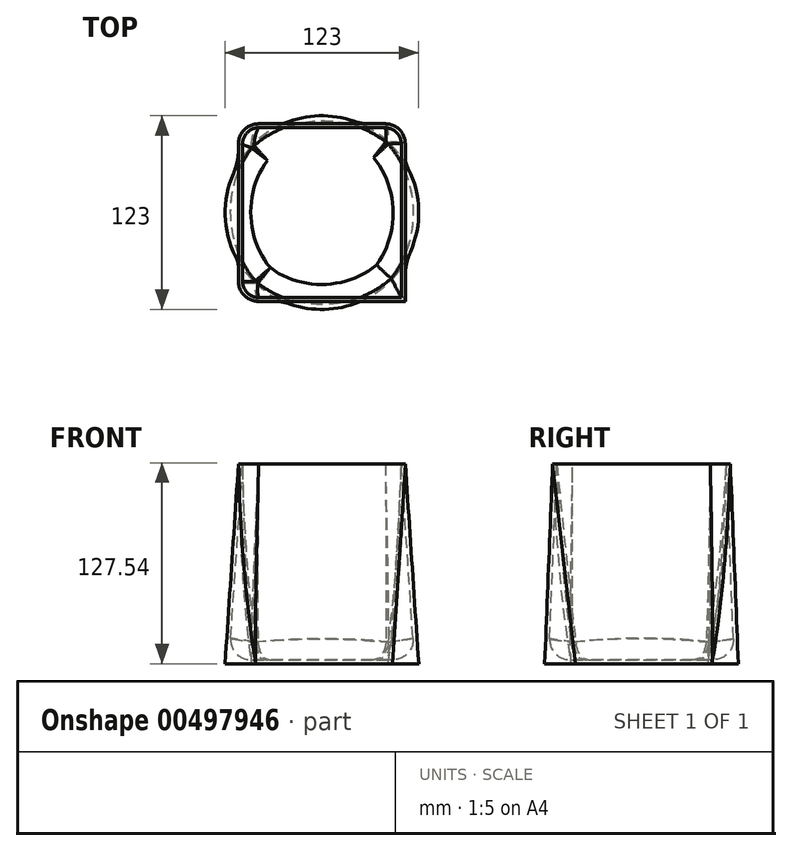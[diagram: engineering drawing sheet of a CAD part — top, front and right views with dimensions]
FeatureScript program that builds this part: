
annotation { "Feature Type Name" : "Feature", "Feature Type Description" : "" }
export const myFeature = defineFeature(function(context is Context, id is Id, definition is map)
    precondition{}
    {
        {
            var Q0;
            Q0=qCreatedBy(makeId("Top.planeOp"),FACE);
            var sketch = newSketch(context, id + "F0", { "sketchPlane" : qUnion([Q0])});
            skCircle(sketch, "E0", {"center": v(0, 0) * mm, "radius": 61.5 * mm});
            skSolve(sketch);
        }
        {
            var Q0;
            Q0=qCreatedBy(makeId("Top.planeOp"),FACE);
            cPlane(context, id + "F1", {"entities" : qUnion([Q0]), "cplaneType" : CPlaneType.OFFSET, "offset" : 127 * mm, "width" : 152.4 * mm, "height" : 152.4 * mm});
        }
        {
            var Q0;
            Q0=qCreatedBy(id+"F1.planeOp",FACE);
            var sketch = newSketch(context, id + "F2", { "sketchPlane" : qUnion([Q0])});
            skLineSegment(sketch, "E1.bottom", {"start": v(52.96, 56.4) * mm, "end": v(-52.96, 56.4) * mm});
            skLineSegment(sketch, "E1.top", {"start": v(52.96, -56.4) * mm, "end": v(-52.96, -56.4) * mm});
            skLineSegment(sketch, "E1.left", {"start": v(52.96, 56.4) * mm, "end": v(52.96, -56.4) * mm});
            skLineSegment(sketch, "E1.right", {"start": v(-52.96, 56.4) * mm, "end": v(-52.96, -56.4) * mm});
            skPoint(sketch, "E1.middle", {"position": v(0, 0) * mm});
            skSolve(sketch);
        }
        {
            var Q0;
            Q0=makeQuery(id+"F2.imprint","IMPRINT",FACE,{"disambiguationData":[TD([[makeQuery(id+"F2.imprint","IMPRINT",EDGE,{"derivedFrom":sQuery(id+"F2.wireOp",EDGE,"E1.bottom")}),1.0]])]});
            var Q1;
            Q1=makeQuery(id+"F0.imprint","IMPRINT",FACE,{"disambiguationData":[TD([[makeQuery(id+"F0.imprint","IMPRINT",EDGE,{"derivedFrom":sQuery(id+"F0.wireOp",EDGE,"E0")}),1.0]])]});
            loft(context, id + "F3", {"sheetProfilesArray" : [{ "sheetProfileEntities" : qUnion([Q0]) }, { "sheetProfileEntities" : qUnion([Q1]) }]});
        }
        {
            var Q0;
            Q0=makeQuery(id+"F3.opLoft","SWEPT_EDGE",EDGE,{"disambiguationData":[OSD([sQuery(id+"F0.wireOp",EDGE,"E0"),sQuery(id+"F2.wireOp",EDGE,"E1.bottom"),sQuery(id+"F2.wireOp",EDGE,"E1.top"),sQuery(id+"F2.wireOp",EDGE,"E1.right")])]});
            var Q1;
            Q1=makeQuery(id+"F3.opLoft","SWEPT_EDGE",EDGE,{"disambiguationData":[OSD([sQuery(id+"F0.wireOp",EDGE,"E0"),sQuery(id+"F2.wireOp",EDGE,"E1.top"),sQuery(id+"F2.wireOp",EDGE,"E1.left"),sQuery(id+"F2.wireOp",EDGE,"E1.right")])]});
            var Q2;
            Q2=makeQuery(id+"F3.opLoft","SWEPT_EDGE",EDGE,{"disambiguationData":[OSD([sQuery(id+"F2.wireOp",EDGE,"E1.bottom"),sQuery(id+"F2.wireOp",EDGE,"E1.left")])]});
            var Q3;
            Q3=makeQuery(id+"F3.opLoft","SWEPT_EDGE",EDGE,{"disambiguationData":[OSD([sQuery(id+"F0.wireOp",EDGE,"E0"),sQuery(id+"F2.wireOp",EDGE,"E1.bottom"),sQuery(id+"F2.wireOp",EDGE,"E1.top"),sQuery(id+"F2.wireOp",EDGE,"E1.left")])]});
            fillet(context, id + "F4", {"entities" : qUnion([Q0, Q1, Q2, Q3]), "radius" : 12.7 * mm, "tangentPropagation" : true, "allowEdgeOverflow" : false});
        }
        {
            var Q0;
            Q0=makeQuery(id+"F3.opLoft","CAP_FACE",FACE,{"disambiguationData":[OSD([makeQuery(id+"F2.imprint","IMPRINT",FACE,{"disambiguationData":[TD([[makeQuery(id+"F2.imprint","IMPRINT",EDGE,{"derivedFrom":sQuery(id+"F2.wireOp",EDGE,"E1.bottom")}),1.0]])]})])],"isStart":true});
            shell(context, id + "F5", {"entities" : qUnion([Q0]), "thickness" : 2.54 * mm});
        }
        {
            var Q0;
            Q0=makeQuery(id+"F5.opShell","OFFSET_FACE",FACE,{"disambiguationData":[OSD([makeQuery(id+"F0.imprint","IMPRINT",FACE,{"disambiguationData":[TD([[makeQuery(id+"F0.imprint","IMPRINT",EDGE,{"derivedFrom":sQuery(id+"F0.wireOp",EDGE,"E0")}),1.0]])]})])]});
            fillet(context, id + "F6", {"entities" : qUnion([Q0]), "radius" : 12.7 * mm, "tangentPropagation" : true, "allowEdgeOverflow" : false});
        }
    });
